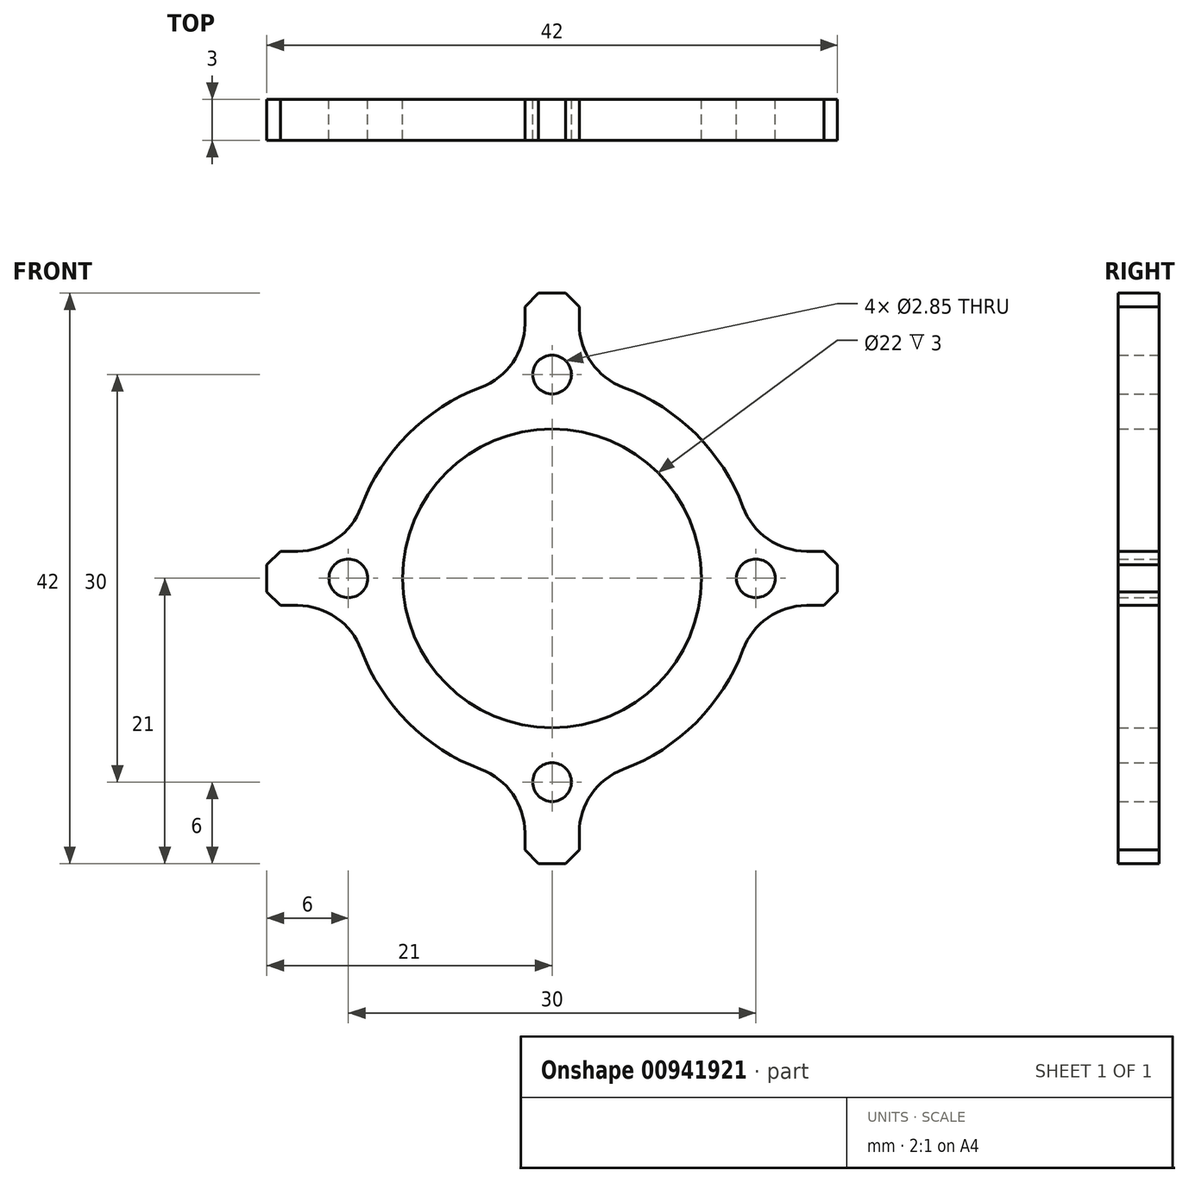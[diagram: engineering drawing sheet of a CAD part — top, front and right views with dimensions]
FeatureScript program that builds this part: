
annotation { "Feature Type Name" : "Feature", "Feature Type Description" : "" }
export const myFeature = defineFeature(function(context is Context, id is Id, definition is map)
    precondition{}
    {
        {
            var Q0;
            Q0=qCreatedBy(makeId("Front.planeOp"),FACE);
            var sketch = newSketch(context, id + "F0", { "sketchPlane" : qUnion([Q0])});
            skCircle(sketch, "E0", {"center": v(0, 0) * mm, "radius": 11 * mm});
            skCircle(sketch, "E1", {"center": v(0, 0) * mm, "radius": 15 * mm});
            skLineSegment(sketch, "E2.bottom", {"start": v(2, 21) * mm, "end": v(-2, 21) * mm});
            skLineSegment(sketch, "E2.top", {"start": v(2, -21) * mm, "end": v(-2, -21) * mm});
            skLineSegment(sketch, "E2.left", {"start": v(2, 21) * mm, "end": v(2, -21) * mm});
            skLineSegment(sketch, "E2.right", {"start": v(-2, 21) * mm, "end": v(-2, -21) * mm});
            skLineSegment(sketch, "E3.bottom", {"start": v(21, -2) * mm, "end": v(-21, -2) * mm});
            skLineSegment(sketch, "E3.top", {"start": v(21, 2) * mm, "end": v(-21, 2) * mm});
            skLineSegment(sketch, "E3.left", {"start": v(21, -2) * mm, "end": v(21, 2) * mm});
            skLineSegment(sketch, "E3.right", {"start": v(-21, -2) * mm, "end": v(-21, 2) * mm});
            skSolve(sketch);
        }
        {
            var Q0;
            Q0 = qSketchRegion(id + "F0", true);
            extrude(context, id + "F1", {"entities" : qUnion([Q0]), "depth" : 3 * mm, "offsetDistance" : 25 * mm});
        }
        {
            var Q0;
            Q0=makeQuery(id+"F1.opExtrude","SWEPT_EDGE",EDGE,{"disambiguationData":[OSD([sQuery(id+"F0.wireOp",EDGE,"E2.bottom"),sQuery(id+"F0.wireOp",EDGE,"E2.right")])]});
            chamfer(context, id + "F2", {"entities" : qUnion([Q0]), "width" : 1 * mm, "tangentPropagation" : true});
        }
        {
            var Q0;
            Q0=makeQuery(id+"F1.opExtrude","SWEPT_EDGE",EDGE,{"disambiguationData":[OSD([sQuery(id+"F0.wireOp",EDGE,"E2.bottom"),sQuery(id+"F0.wireOp",EDGE,"E2.left")])]});
            chamfer(context, id + "F3", {"entities" : qUnion([Q0]), "width" : 1 * mm, "tangentPropagation" : true});
        }
        {
            var Q0;
            Q0=makeQuery(id+"F1.opExtrude","SWEPT_EDGE",EDGE,{"disambiguationData":[OSD([sQuery(id+"F0.wireOp",EDGE,"E3.top"),sQuery(id+"F0.wireOp",EDGE,"E3.left")])]});
            var Q1;
            Q1=makeQuery(id+"F1.opExtrude","SWEPT_EDGE",EDGE,{"disambiguationData":[OSD([sQuery(id+"F0.wireOp",EDGE,"E3.bottom"),sQuery(id+"F0.wireOp",EDGE,"E3.left")])]});
            chamfer(context, id + "F4", {"entities" : qUnion([Q0, Q1]), "width" : 1 * mm, "tangentPropagation" : true});
        }
        {
            var Q0;
            Q0=makeQuery(id+"F1.opExtrude","SWEPT_EDGE",EDGE,{"disambiguationData":[OSD([sQuery(id+"F0.wireOp",EDGE,"E2.top"),sQuery(id+"F0.wireOp",EDGE,"E2.left")])]});
            var Q1;
            Q1=makeQuery(id+"F1.opExtrude","SWEPT_EDGE",EDGE,{"disambiguationData":[OSD([sQuery(id+"F0.wireOp",EDGE,"E2.top"),sQuery(id+"F0.wireOp",EDGE,"E2.right")])]});
            chamfer(context, id + "F5", {"entities" : qUnion([Q0, Q1]), "width" : 1 * mm, "tangentPropagation" : true});
        }
        {
            var Q0;
            Q0=makeQuery(id+"F1.opExtrude","SWEPT_EDGE",EDGE,{"disambiguationData":[OSD([sQuery(id+"F0.wireOp",EDGE,"E3.top"),sQuery(id+"F0.wireOp",EDGE,"E3.right")])]});
            var Q1;
            Q1=makeQuery(id+"F1.opExtrude","SWEPT_EDGE",EDGE,{"disambiguationData":[OSD([sQuery(id+"F0.wireOp",EDGE,"E3.bottom"),sQuery(id+"F0.wireOp",EDGE,"E3.right")])]});
            chamfer(context, id + "F6", {"entities" : qUnion([Q0, Q1]), "width" : 1 * mm, "tangentPropagation" : true});
        }
        {
            var Q0;
            Q0=qCreatedBy(makeId("Front.planeOp"),FACE);
            var sketch = newSketch(context, id + "F7", { "sketchPlane" : qUnion([Q0])});
            skCircle(sketch, "E4", {"center": v(0, 15) * mm, "radius": 1.43 * mm});
            skCircle(sketch, "E5", {"center": v(15, 0) * mm, "radius": 1.43 * mm});
            skCircle(sketch, "E6", {"center": v(-15, 0) * mm, "radius": 1.43 * mm});
            skCircle(sketch, "E7", {"center": v(0, -15) * mm, "radius": 1.43 * mm});
            skSolve(sketch);
        }
        {
            var Q0;
            Q0 = qSketchRegion(id + "F7", true);
            extrude(context, id + "F8", {"entities" : qUnion([Q0]), "operationType" : NewBodyOperationType.REMOVE, "endBound" : BoundingType.THROUGH_ALL, "depth" : 25 * mm, "offsetDistance" : 25 * mm});
        }
        {
            var Q0;
            {var subQ0=sQuery(id+"F0.wireOp",EDGE,"E2.right");var subQ1=sQuery(id+"F0.wireOp",EDGE,"E1");Q0=makeQuery(id+"F1.opExtrude","SWEPT_EDGE",EDGE,{"disambiguationData":[OSD([subQ1,subQ0]),TDD([makeQuery(id+"F0.imprint","INTERSECT",VERTEX,{"disambiguationData":[OD(0.0)],"derivedFrom":[subQ1,subQ0]})])]});}
            fillet(context, id + "F9", {"entities" : qUnion([Q0]), "radius" : 5 * mm, "tangentPropagation" : true, "allowEdgeOverflow" : false});
        }
        {
            var Q0;
            {var subQ0=sQuery(id+"F0.wireOp",EDGE,"E2.left");var subQ1=sQuery(id+"F0.wireOp",EDGE,"E1");Q0=makeQuery(id+"F1.opExtrude","SWEPT_EDGE",EDGE,{"disambiguationData":[OSD([subQ1,subQ0]),TDD([makeQuery(id+"F0.imprint","INTERSECT",VERTEX,{"disambiguationData":[OD(0.0)],"derivedFrom":[subQ1,subQ0]})])]});}
            fillet(context, id + "F10", {"entities" : qUnion([Q0]), "radius" : 5 * mm, "tangentPropagation" : true, "allowEdgeOverflow" : false});
        }
        {
            var Q0;
            {var subQ0=sQuery(id+"F0.wireOp",EDGE,"E3.bottom");var subQ1=sQuery(id+"F0.wireOp",EDGE,"E1");Q0=makeQuery(id+"F1.opExtrude","SWEPT_EDGE",EDGE,{"disambiguationData":[OSD([subQ1,subQ0]),TDD([makeQuery(id+"F0.imprint","INTERSECT",VERTEX,{"disambiguationData":[OD(1.0)],"derivedFrom":[subQ1,subQ0]})])]});}
            fillet(context, id + "F11", {"entities" : qUnion([Q0]), "radius" : 5 * mm, "tangentPropagation" : true, "allowEdgeOverflow" : false});
        }
        {
            var Q0;
            {var subQ0=sQuery(id+"F0.wireOp",EDGE,"E2.right");var subQ1=sQuery(id+"F0.wireOp",EDGE,"E1");Q0=makeQuery(id+"F1.opExtrude","SWEPT_EDGE",EDGE,{"disambiguationData":[OSD([subQ1,subQ0]),TDD([makeQuery(id+"F0.imprint","INTERSECT",VERTEX,{"disambiguationData":[OD(1.0)],"derivedFrom":[subQ1,subQ0]})])]});}
            fillet(context, id + "F12", {"entities" : qUnion([Q0]), "radius" : 5 * mm, "tangentPropagation" : true, "allowEdgeOverflow" : false});
        }
        {
            var Q0;
            {var subQ0=sQuery(id+"F0.wireOp",EDGE,"E2.left");var subQ1=sQuery(id+"F0.wireOp",EDGE,"E1");Q0=makeQuery(id+"F1.opExtrude","SWEPT_EDGE",EDGE,{"disambiguationData":[OSD([subQ1,subQ0]),TDD([makeQuery(id+"F0.imprint","INTERSECT",VERTEX,{"disambiguationData":[OD(1.0)],"derivedFrom":[subQ1,subQ0]})])]});}
            fillet(context, id + "F13", {"entities" : qUnion([Q0]), "radius" : 5 * mm, "tangentPropagation" : true, "allowEdgeOverflow" : false});
        }
        {
            var Q0;
            {var subQ0=sQuery(id+"F0.wireOp",EDGE,"E3.top");var subQ1=sQuery(id+"F0.wireOp",EDGE,"E1");Q0=makeQuery(id+"F1.opExtrude","SWEPT_EDGE",EDGE,{"disambiguationData":[OSD([subQ1,subQ0]),TDD([makeQuery(id+"F0.imprint","INTERSECT",VERTEX,{"disambiguationData":[OD(0.0)],"derivedFrom":[subQ1,subQ0]})])]});}
            fillet(context, id + "F14", {"entities" : qUnion([Q0]), "radius" : 5 * mm, "tangentPropagation" : true, "allowEdgeOverflow" : false});
        }
        {
            var Q0;
            {var subQ0=sQuery(id+"F0.wireOp",EDGE,"E3.bottom");var subQ1=sQuery(id+"F0.wireOp",EDGE,"E1");Q0=makeQuery(id+"F1.opExtrude","SWEPT_EDGE",EDGE,{"disambiguationData":[OSD([subQ1,subQ0]),TDD([makeQuery(id+"F0.imprint","INTERSECT",VERTEX,{"disambiguationData":[OD(0.0)],"derivedFrom":[subQ1,subQ0]})])]});}
            fillet(context, id + "F15", {"entities" : qUnion([Q0]), "radius" : 5 * mm, "tangentPropagation" : true, "allowEdgeOverflow" : false});
        }
        {
            var Q0;
            {var subQ0=sQuery(id+"F0.wireOp",EDGE,"E3.top");var subQ1=sQuery(id+"F0.wireOp",EDGE,"E1");Q0=makeQuery(id+"F1.opExtrude","SWEPT_EDGE",EDGE,{"disambiguationData":[OSD([subQ1,subQ0]),TDD([makeQuery(id+"F0.imprint","INTERSECT",VERTEX,{"disambiguationData":[OD(1.0)],"derivedFrom":[subQ1,subQ0]})])]});}
            fillet(context, id + "F16", {"entities" : qUnion([Q0]), "radius" : 5 * mm, "tangentPropagation" : true, "allowEdgeOverflow" : false});
        }
    });
